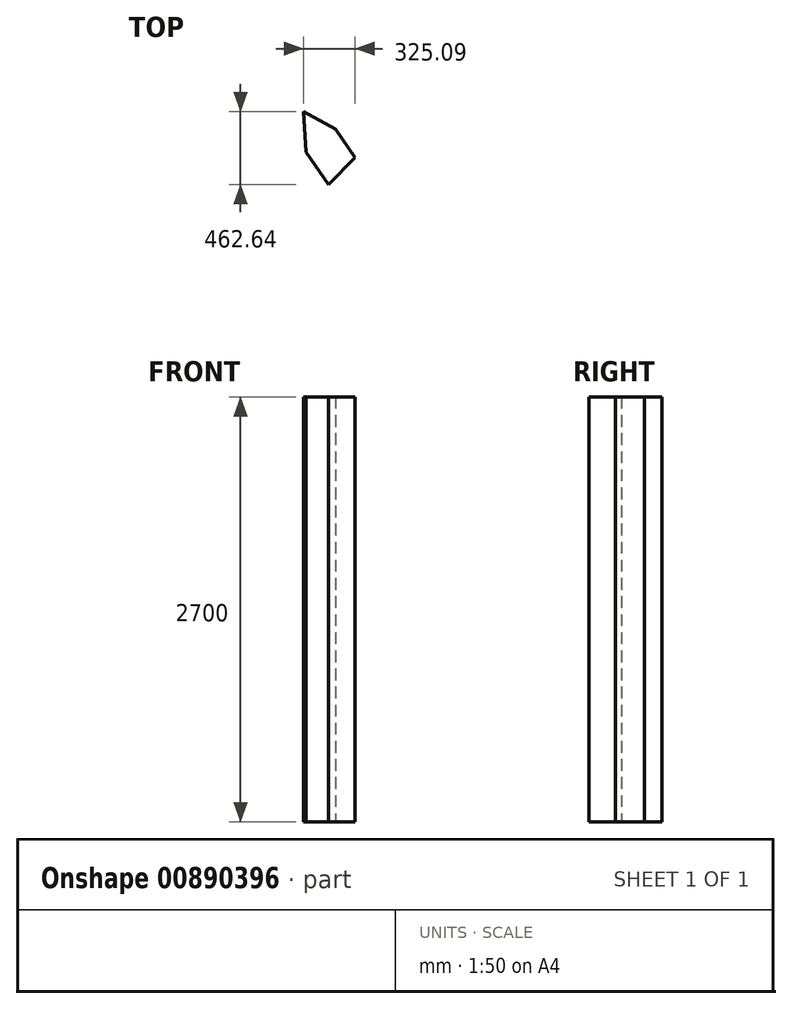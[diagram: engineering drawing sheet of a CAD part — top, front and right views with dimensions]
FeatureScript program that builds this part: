
annotation { "Feature Type Name" : "Feature", "Feature Type Description" : "" }
export const myFeature = defineFeature(function(context is Context, id is Id, definition is map)
    precondition{}
    {
        {
            var Q0;
            Q0=qCreatedBy(makeId("Top.planeOp"),FACE);
            var sketch = newSketch(context, id + "F0", { "sketchPlane" : qUnion([Q0])});
            skLineSegment(sketch, "E0", {"start": v(-5.12, 17.38) * mm, "end": v(-21.24, 274.81) * mm});
            skLineSegment(sketch, "E1", {"start": v(-21.24, 274.81) * mm, "end": v(180.7, 164.24) * mm});
            skLineSegment(sketch, "E2", {"start": v(180.7, 164.24) * mm, "end": v(303.85, -18.5) * mm});
            skLineSegment(sketch, "E3", {"start": v(303.85, -18.5) * mm, "end": v(135.73, -187.83) * mm});
            skLineSegment(sketch, "E4", {"start": v(135.73, -187.83) * mm, "end": v(-5.12, 17.38) * mm});
            skLineSegment(sketch, "E5", {"start": v(540.9, -260.48) * mm, "end": v(332.03, 231.08) * mm});
            skSolve(sketch);
        }
        {
            var Q0;
            Q0 = qSketchRegion(id + "F0", true);
            extrude(context, id + "F1", {"entities" : qUnion([Q0]), "depth" : 2700 * mm, "offsetDistance" : 25 * mm});
        }
    });
